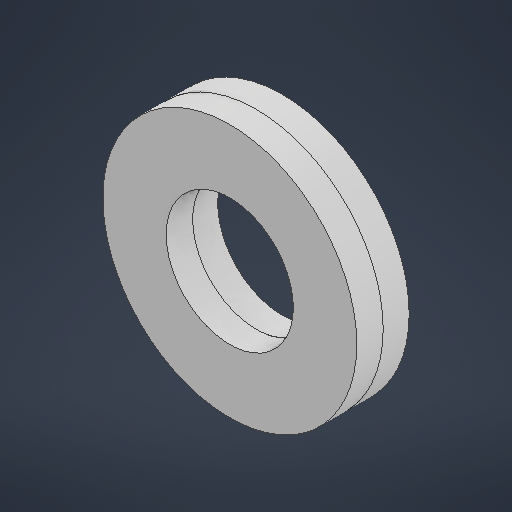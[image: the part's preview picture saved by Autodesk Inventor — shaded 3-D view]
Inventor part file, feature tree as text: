
AUTODESK INVENTOR PART (.ipt)
format: ipt  version: 2025 (Build 290162000, 162)  size: 202,240 bytes
history: native  units: in
note: dims shown in document units (in); Inventor stores cm internally (conversion verified against a paired STEP export)
features: revolve x2
ambient origin geometry x8: Origin, YZ Plane, XZ Plane, XY Plane, X Axis, Y Axis, Z Axis, Center Point
bodies: Solid1 (feature_tree), Solid2 (feature_tree)
feature tree (2):
  revolve  "Revolve1"  [1 undecoded]
  revolve  "Revolve2"  [1 undecoded]
note: 2 required parameter values undecoded (feature->parameter linkage not recoverable at this tier; creation-order binding heuristic only, values carry confidence <= 0.55)
